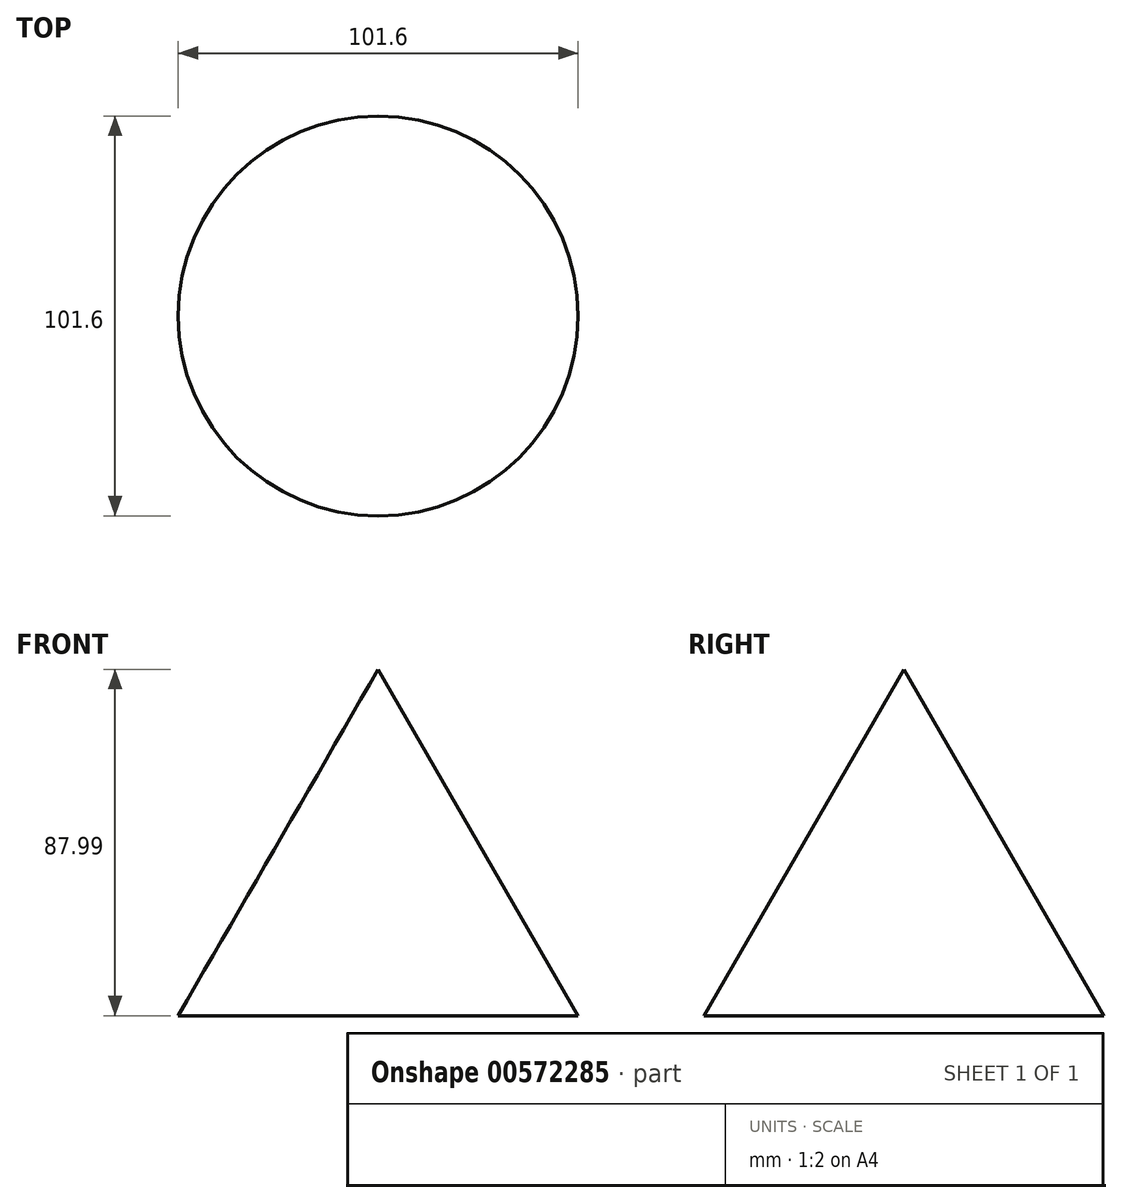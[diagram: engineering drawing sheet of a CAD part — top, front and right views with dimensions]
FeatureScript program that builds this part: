
annotation { "Feature Type Name" : "Feature", "Feature Type Description" : "" }
export const myFeature = defineFeature(function(context is Context, id is Id, definition is map)
    precondition{}
    {
        {
            var Q0;
            Q0=qCreatedBy(makeId("Front.planeOp"),FACE);
            var sketch = newSketch(context, id + "F0", { "sketchPlane" : qUnion([Q0])});
            skLineSegment(sketch, "E0", {"start": v(0, 0) * mm, "end": v(50.8, 0) * mm});
            skLineSegment(sketch, "E1", {"start": v(50.8, 0) * mm, "end": v(0, 87.99) * mm});
            skLineSegment(sketch, "E2", {"start": v(0, 87.99) * mm, "end": v(0, 0) * mm});
            skSolve(sketch);
        }
        {
            var Q0;
            Q0=makeQuery(id+"F0.imprint","IMPRINT",FACE,{"disambiguationData":[TD([[makeQuery(id+"F0.imprint","IMPRINT",EDGE,{"derivedFrom":sQuery(id+"F0.wireOp",EDGE,"E0")}),1.0]])]});
            var Q1;
            Q1=sQuery(id+"F0.wireOp",EDGE,"E2");
            revolve(context, id + "F1", {"entities" : qUnion([Q0]), "axis" : qUnion([Q1]), "revolveType" : RevolveType.FULL});
        }
    });
